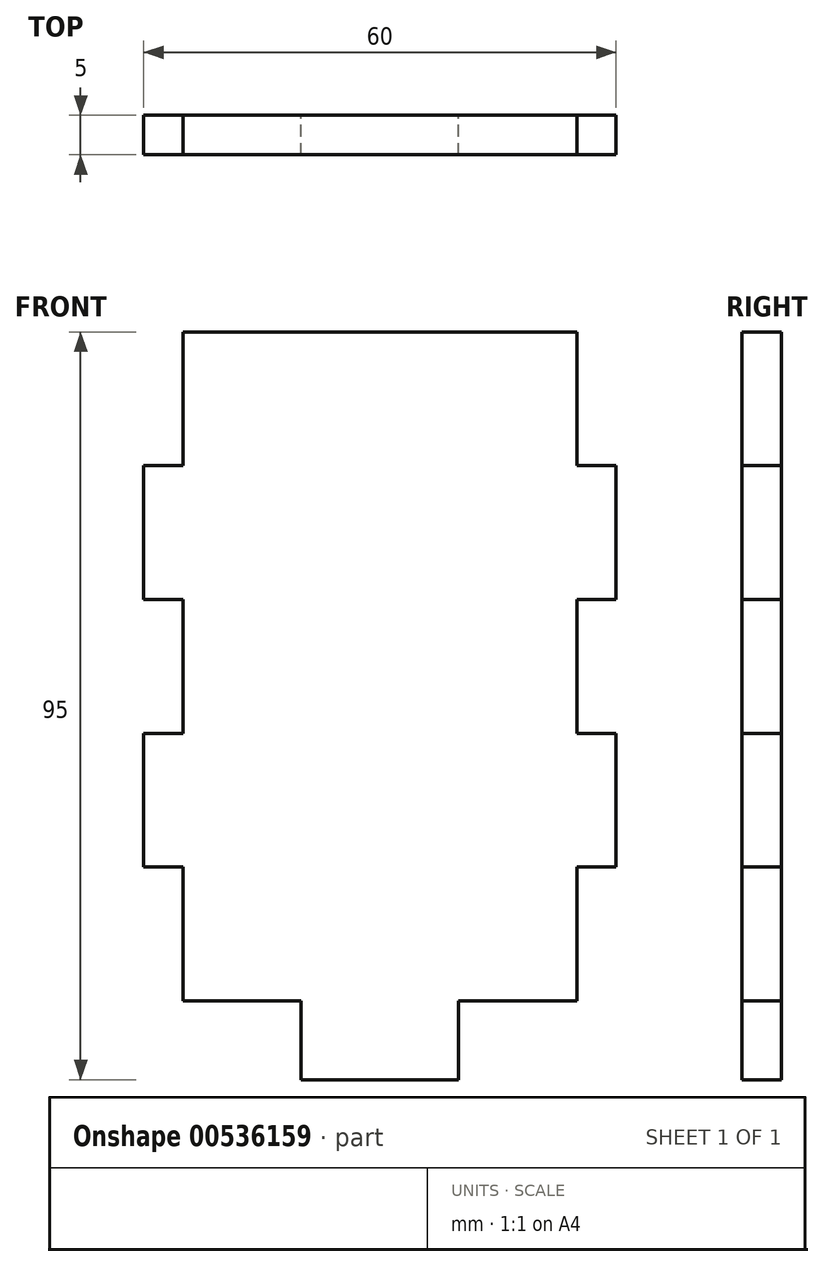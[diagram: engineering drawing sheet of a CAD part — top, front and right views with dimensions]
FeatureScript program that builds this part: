
annotation { "Feature Type Name" : "Feature", "Feature Type Description" : "" }
export const myFeature = defineFeature(function(context is Context, id is Id, definition is map)
    precondition{}
    {
        {
            var Q0;
            Q0=qCreatedBy(makeId("Front.planeOp"),FACE);
            var sketch = newSketch(context, id + "F0", { "sketchPlane" : qUnion([Q0])});
            skLineSegment(sketch, "E0.bottom", {"start": v(25, 58.16) * mm, "end": v(-25, 58.16) * mm});
            skLineSegment(sketch, "E0.top", {"start": v(25, -26.84) * mm, "end": v(10, -26.84) * mm});
            skLineSegment(sketch, "E0.left", {"start": v(25, 58.16) * mm, "end": v(25, 41.16) * mm});
            skLineSegment(sketch, "E0.right", {"start": v(-25, 58.16) * mm, "end": v(-25, 41.16) * mm});
            skPoint(sketch, "E0.middle", {"position": v(0, 15.66) * mm});
            skLineSegment(sketch, "E1", {"start": v(-30, 58.16) * mm, "end": v(-30, -31.84) * mm, "construction": true});
            skLineSegment(sketch, "E2", {"start": v(30, -31.84) * mm, "end": v(30, 58.16) * mm, "construction": true});
            skLineSegment(sketch, "E3", {"start": v(-10, -26.84) * mm, "end": v(-10, -31.84) * mm});
            skLineSegment(sketch, "E4", {"start": v(-10, -36.84) * mm, "end": v(10, -36.84) * mm});
            skLineSegment(sketch, "E5", {"start": v(10, -26.84) * mm, "end": v(10, -31.84) * mm});
            skLineSegment(sketch, "E6", {"start": v(-25, -9.84) * mm, "end": v(-30, -9.84) * mm});
            skLineSegment(sketch, "E7", {"start": v(-30, -9.84) * mm, "end": v(-30, 7.16) * mm});
            skLineSegment(sketch, "E8", {"start": v(-30, 7.16) * mm, "end": v(-25, 7.16) * mm});
            skLineSegment(sketch, "E9", {"start": v(-25, 24.16) * mm, "end": v(-30, 24.16) * mm});
            skLineSegment(sketch, "E10", {"start": v(-30, 24.16) * mm, "end": v(-30, 41.16) * mm});
            skLineSegment(sketch, "E11", {"start": v(-30, 41.16) * mm, "end": v(-25, 41.16) * mm});
            skLineSegment(sketch, "E12.trimOffspring", {"start": v(-25, 24.16) * mm, "end": v(-25, 7.16) * mm});
            skLineSegment(sketch, "E13.trimOffspring", {"start": v(-25, -9.84) * mm, "end": v(-25, -26.84) * mm});
            skLineSegment(sketch, "E14.MirrorCS", {"start": v(30, 41.16) * mm, "end": v(25, 41.16) * mm});
            skLineSegment(sketch, "E15.MirrorCS", {"start": v(25, 24.16) * mm, "end": v(30, 24.16) * mm});
            skLineSegment(sketch, "E16.MirrorCS", {"start": v(30, 7.16) * mm, "end": v(25, 7.16) * mm});
            skLineSegment(sketch, "E17.MirrorCS", {"start": v(25, -9.84) * mm, "end": v(30, -9.84) * mm});
            skLineSegment(sketch, "E18", {"start": v(30, 41.16) * mm, "end": v(30, 24.16) * mm});
            skLineSegment(sketch, "E19", {"start": v(30, 7.16) * mm, "end": v(30, -9.84) * mm});
            skLineSegment(sketch, "E20.trimOffspring", {"start": v(25, 24.16) * mm, "end": v(25, 7.16) * mm});
            skLineSegment(sketch, "E21.trimOffspring", {"start": v(25, -9.84) * mm, "end": v(25, -26.84) * mm});
            skLineSegment(sketch, "E22.trimOffspring", {"start": v(-10, -26.84) * mm, "end": v(-25, -26.84) * mm});
            skPoint(sketch, "E23.start.orphan", {"position": v(30, -36.84) * mm});
            skLineSegment(sketch, "E24", {"start": v(-10, -31.84) * mm, "end": v(-10, -36.84) * mm});
            skPoint(sketch, "E24.endSnap0", {"position": v(0, -36.84) * mm});
            skLineSegment(sketch, "E25", {"start": v(10, -31.84) * mm, "end": v(10, -36.84) * mm});
            skPoint(sketch, "E26.end.orphan", {"position": v(-25, -31.84) * mm});
            skPoint(sketch, "E27.orphan", {"position": v(-25, -36.84) * mm});
            skPoint(sketch, "E28.end.orphan", {"position": v(25, -36.84) * mm});
            skPoint(sketch, "E29.start.orphan", {"position": v(25, -31.84) * mm});
            skSolve(sketch);
        }
        {
            var Q0;
            Q0 = qSketchRegion(id + "F0", true);
            extrude(context, id + "F1", {"entities" : qUnion([Q0]), "depth" : 5 * mm, "offsetDistance" : 25 * mm});
        }
    });
